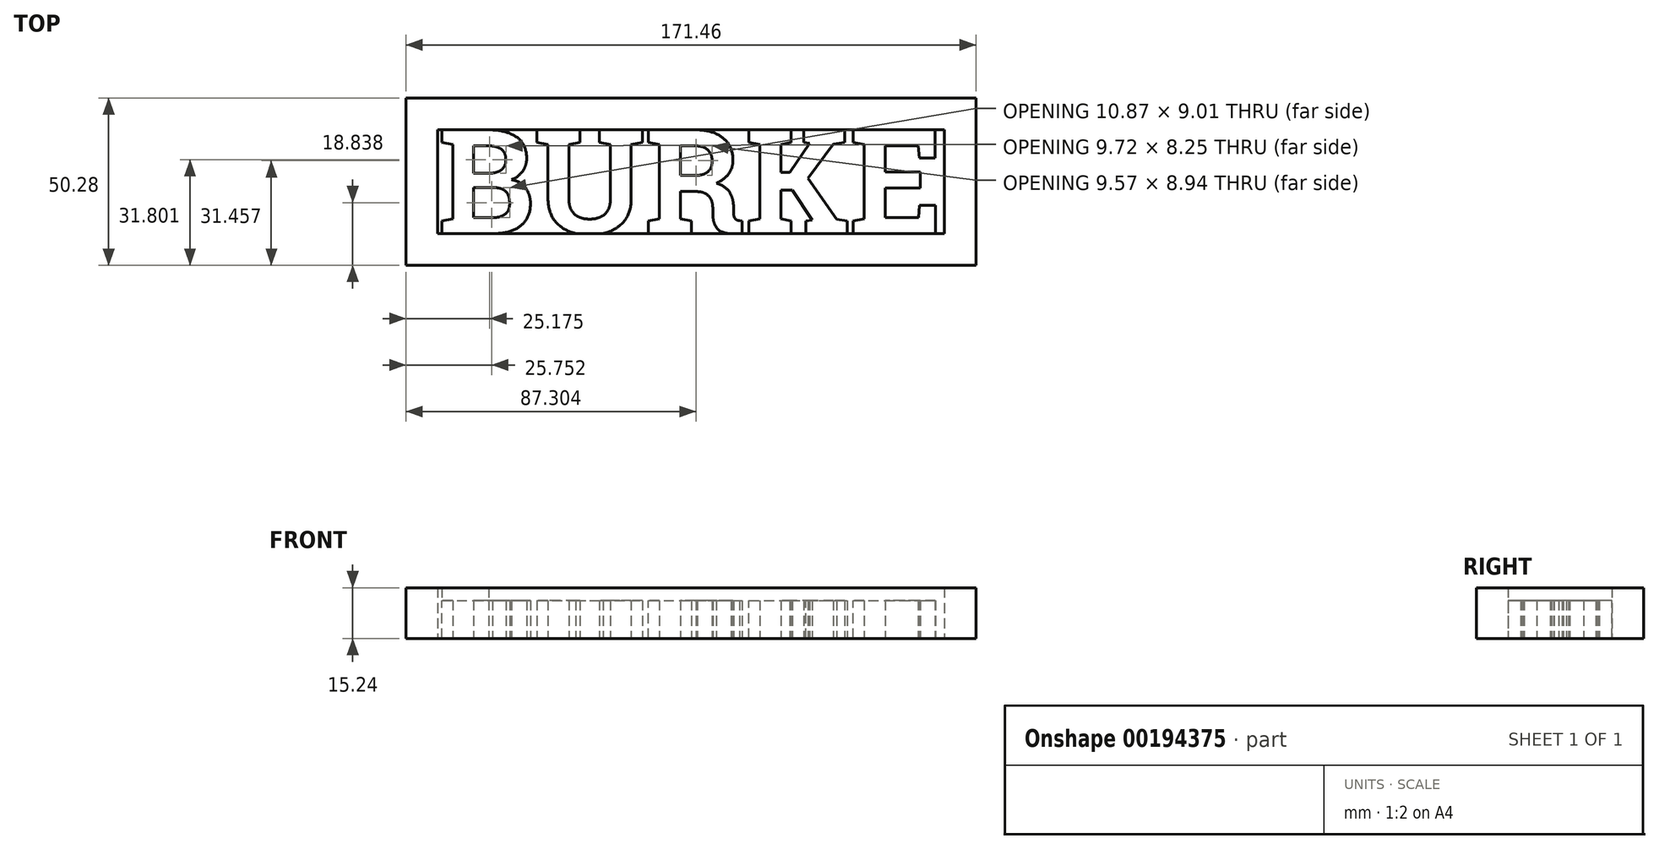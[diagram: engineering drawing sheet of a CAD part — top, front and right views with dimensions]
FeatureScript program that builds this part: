
annotation { "Feature Type Name" : "Feature", "Feature Type Description" : "" }
export const myFeature = defineFeature(function(context is Context, id is Id, definition is map)
    precondition{}
    {
        {
            var Q0;
            Q0=qCreatedBy(makeId("Top.planeOp"),FACE);
            var sketch = newSketch(context, id + "F0", { "sketchPlane" : qUnion([Q0])});
            skLineSegment(sketch, "E0.bottom", {"start": v(0, 0) * mm, "end": v(152.4, 0) * mm});
            skLineSegment(sketch, "E0.top", {"start": v(0, 9.53) * mm, "end": v(152.4, 9.53) * mm});
            skLineSegment(sketch, "E0.left", {"start": v(0, 0) * mm, "end": v(0, 9.53) * mm});
            skLineSegment(sketch, "E0.right", {"start": v(152.4, 0) * mm, "end": v(152.4, 9.53) * mm});
            skText(sketch, "E1", { "text": "BURKE", "fontName": "RobotoSlab-Bold.ttf"});
            const initialGuessF0  = {"E1": [0, 0.00953, 1, 0, 0.03162]};
            skSetInitialGuess(sketch, initialGuessF0);
            skSolve(sketch);
        }
        {
            var Q0;
            Q0=qSketchRegion(id+"F0",true);
            extrude(context, id + "F1", {"entities" : qUnion([Q0]), "depth" : 11.43 * mm});
        }
        {
            var Q0;
            Q0=makeQuery(id+"F1.opExtrude","CAP_FACE",FACE,{"disambiguationData":[OSD([sQuery(id+"F0.wireOp",EDGE,"E0.bottom"),sQuery(id+"F0.wireOp",EDGE,"E0.top"),sQuery(id+"F0.wireOp",EDGE,"E0.left"),sQuery(id+"F0.wireOp",EDGE,"E0.right"),sQuery(id+"F0.wireOp",EDGE,"E1.sketch_text.stroke-0"),sQuery(id+"F0.wireOp",EDGE,"E1.sketch_text.stroke-1"),sQuery(id+"F0.wireOp",EDGE,"E1.sketch_text.stroke-2"),sQuery(id+"F0.wireOp",EDGE,"E1.sketch_text.stroke-3"),sQuery(id+"F0.wireOp",EDGE,"E1.sketch_text.stroke-4"),sQuery(id+"F0.wireOp",EDGE,"E1.sketch_text.stroke-5"),sQuery(id+"F0.wireOp",EDGE,"E1.sketch_text.stroke-6"),sQuery(id+"F0.wireOp",EDGE,"E1.sketch_text.stroke-7"),sQuery(id+"F0.wireOp",EDGE,"E1.sketch_text.stroke-8"),sQuery(id+"F0.wireOp",EDGE,"E1.sketch_text.stroke-9"),sQuery(id+"F0.wireOp",EDGE,"E1.sketch_text.stroke-10"),sQuery(id+"F0.wireOp",EDGE,"E1.sketch_text.stroke-11"),sQuery(id+"F0.wireOp",EDGE,"E1.sketch_text.stroke-12"),sQuery(id+"F0.wireOp",EDGE,"E1.sketch_text.stroke-13"),sQuery(id+"F0.wireOp",EDGE,"E1.sketch_text.stroke-14"),sQuery(id+"F0.wireOp",EDGE,"E1.sketch_text.stroke-15"),sQuery(id+"F0.wireOp",EDGE,"E1.sketch_text.stroke-16"),sQuery(id+"F0.wireOp",EDGE,"E1.sketch_text.stroke-17"),sQuery(id+"F0.wireOp",EDGE,"E1.sketch_text.stroke-18"),sQuery(id+"F0.wireOp",EDGE,"E1.sketch_text.stroke-19"),sQuery(id+"F0.wireOp",EDGE,"E1.sketch_text.stroke-20"),sQuery(id+"F0.wireOp",EDGE,"E1.sketch_text.stroke-21"),sQuery(id+"F0.wireOp",EDGE,"E1.sketch_text.stroke-22"),sQuery(id+"F0.wireOp",EDGE,"E1.sketch_text.stroke-23"),sQuery(id+"F0.wireOp",EDGE,"E1.sketch_text.stroke-24"),sQuery(id+"F0.wireOp",EDGE,"E1.sketch_text.stroke-25"),sQuery(id+"F0.wireOp",EDGE,"E1.sketch_text.stroke-26"),sQuery(id+"F0.wireOp",EDGE,"E1.sketch_text.stroke-27"),sQuery(id+"F0.wireOp",EDGE,"E1.sketch_text.stroke-28"),sQuery(id+"F0.wireOp",EDGE,"E1.sketch_text.stroke-29"),sQuery(id+"F0.wireOp",EDGE,"E1.sketch_text.stroke-30"),sQuery(id+"F0.wireOp",EDGE,"E1.sketch_text.stroke-31"),sQuery(id+"F0.wireOp",EDGE,"E1.sketch_text.stroke-32"),sQuery(id+"F0.wireOp",EDGE,"E1.sketch_text.stroke-33"),sQuery(id+"F0.wireOp",EDGE,"E1.sketch_text.stroke-34"),sQuery(id+"F0.wireOp",EDGE,"E1.sketch_text.stroke-35"),sQuery(id+"F0.wireOp",EDGE,"E1.sketch_text.stroke-36"),sQuery(id+"F0.wireOp",EDGE,"E1.sketch_text.stroke-37"),sQuery(id+"F0.wireOp",EDGE,"E1.sketch_text.stroke-38"),sQuery(id+"F0.wireOp",EDGE,"E1.sketch_text.stroke-39"),sQuery(id+"F0.wireOp",EDGE,"E1.sketch_text.stroke-40"),sQuery(id+"F0.wireOp",EDGE,"E1.sketch_text.stroke-42"),sQuery(id+"F0.wireOp",EDGE,"E1.sketch_text.stroke-43"),sQuery(id+"F0.wireOp",EDGE,"E1.sketch_text.stroke-44"),sQuery(id+"F0.wireOp",EDGE,"E1.sketch_text.stroke-45"),sQuery(id+"F0.wireOp",EDGE,"E1.sketch_text.stroke-46"),sQuery(id+"F0.wireOp",EDGE,"E1.sketch_text.stroke-47"),sQuery(id+"F0.wireOp",EDGE,"E1.sketch_text.stroke-48"),sQuery(id+"F0.wireOp",EDGE,"E1.sketch_text.stroke-50"),sQuery(id+"F0.wireOp",EDGE,"E1.sketch_text.stroke-51"),sQuery(id+"F0.wireOp",EDGE,"E1.sketch_text.stroke-52"),sQuery(id+"F0.wireOp",EDGE,"E1.sketch_text.stroke-53"),sQuery(id+"F0.wireOp",EDGE,"E1.sketch_text.stroke-54"),sQuery(id+"F0.wireOp",EDGE,"E1.sketch_text.stroke-55"),sQuery(id+"F0.wireOp",EDGE,"E1.sketch_text.stroke-56"),sQuery(id+"F0.wireOp",EDGE,"E1.sketch_text.stroke-57"),sQuery(id+"F0.wireOp",EDGE,"E1.sketch_text.stroke-58"),sQuery(id+"F0.wireOp",EDGE,"E1.sketch_text.stroke-59"),sQuery(id+"F0.wireOp",EDGE,"E1.sketch_text.stroke-60"),sQuery(id+"F0.wireOp",EDGE,"E1.sketch_text.stroke-62"),sQuery(id+"F0.wireOp",EDGE,"E1.sketch_text.stroke-63"),sQuery(id+"F0.wireOp",EDGE,"E1.sketch_text.stroke-64"),sQuery(id+"F0.wireOp",EDGE,"E1.sketch_text.stroke-65"),sQuery(id+"F0.wireOp",EDGE,"E1.sketch_text.stroke-66"),sQuery(id+"F0.wireOp",EDGE,"E1.sketch_text.stroke-67"),sQuery(id+"F0.wireOp",EDGE,"E1.sketch_text.stroke-68"),sQuery(id+"F0.wireOp",EDGE,"E1.sketch_text.stroke-69"),sQuery(id+"F0.wireOp",EDGE,"E1.sketch_text.stroke-70"),sQuery(id+"F0.wireOp",EDGE,"E1.sketch_text.stroke-71"),sQuery(id+"F0.wireOp",EDGE,"E1.sketch_text.stroke-72"),sQuery(id+"F0.wireOp",EDGE,"E1.sketch_text.stroke-73"),sQuery(id+"F0.wireOp",EDGE,"E1.sketch_text.stroke-75"),sQuery(id+"F0.wireOp",EDGE,"E1.sketch_text.stroke-76"),sQuery(id+"F0.wireOp",EDGE,"E1.sketch_text.stroke-77"),sQuery(id+"F0.wireOp",EDGE,"E1.sketch_text.stroke-78"),sQuery(id+"F0.wireOp",EDGE,"E1.sketch_text.stroke-79"),sQuery(id+"F0.wireOp",EDGE,"E1.sketch_text.stroke-80"),sQuery(id+"F0.wireOp",EDGE,"E1.sketch_text.stroke-81"),sQuery(id+"F0.wireOp",EDGE,"E1.sketch_text.stroke-82"),sQuery(id+"F0.wireOp",EDGE,"E1.sketch_text.stroke-83"),sQuery(id+"F0.wireOp",EDGE,"E1.sketch_text.stroke-84"),sQuery(id+"F0.wireOp",EDGE,"E1.sketch_text.stroke-85"),sQuery(id+"F0.wireOp",EDGE,"E1.sketch_text.stroke-86"),sQuery(id+"F0.wireOp",EDGE,"E1.sketch_text.stroke-87"),sQuery(id+"F0.wireOp",EDGE,"E1.sketch_text.stroke-88")])],"isStart":false});
            var sketch = newSketch(context, id + "F2", { "sketchPlane" : qUnion([Q0])});
            skLineSegment(sketch, "E2.bottom", {"start": v(0, 0) * mm, "end": v(152.4, 0) * mm});
            skLineSegment(sketch, "E2.top", {"start": v(0, 9.53) * mm, "end": v(152.4, 9.53) * mm});
            skLineSegment(sketch, "E2.left", {"start": v(0, 0) * mm, "end": v(0, 9.53) * mm});
            skLineSegment(sketch, "E2.right", {"start": v(152.4, 0) * mm, "end": v(152.4, 9.53) * mm});
            skSolve(sketch);
        }
        {
            var Q0;
            Q0=qSketchRegion(id+"F2",true);
            extrude(context, id + "F3", {"entities" : qUnion([Q0]), "operationType" : NewBodyOperationType.ADD, "depth" : 3.8 * mm});
        }
        {
            var Q0;
            Q0=makeQuery(id+"F1.opExtrude","CAP_FACE",FACE,{"disambiguationData":[OSD([sQuery(id+"F0.wireOp",EDGE,"E0.bottom"),sQuery(id+"F0.wireOp",EDGE,"E0.top"),sQuery(id+"F0.wireOp",EDGE,"E0.left"),sQuery(id+"F0.wireOp",EDGE,"E0.right"),sQuery(id+"F0.wireOp",EDGE,"E1.sketch_text.stroke-0"),sQuery(id+"F0.wireOp",EDGE,"E1.sketch_text.stroke-1"),sQuery(id+"F0.wireOp",EDGE,"E1.sketch_text.stroke-2"),sQuery(id+"F0.wireOp",EDGE,"E1.sketch_text.stroke-3"),sQuery(id+"F0.wireOp",EDGE,"E1.sketch_text.stroke-4"),sQuery(id+"F0.wireOp",EDGE,"E1.sketch_text.stroke-5"),sQuery(id+"F0.wireOp",EDGE,"E1.sketch_text.stroke-7"),sQuery(id+"F0.wireOp",EDGE,"E1.sketch_text.stroke-8"),sQuery(id+"F0.wireOp",EDGE,"E1.sketch_text.stroke-9"),sQuery(id+"F0.wireOp",EDGE,"E1.sketch_text.stroke-10"),sQuery(id+"F0.wireOp",EDGE,"E1.sketch_text.stroke-11"),sQuery(id+"F0.wireOp",EDGE,"E1.sketch_text.stroke-12"),sQuery(id+"F0.wireOp",EDGE,"E1.sketch_text.stroke-13"),sQuery(id+"F0.wireOp",EDGE,"E1.sketch_text.stroke-15"),sQuery(id+"F0.wireOp",EDGE,"E1.sketch_text.stroke-16"),sQuery(id+"F0.wireOp",EDGE,"E1.sketch_text.stroke-17"),sQuery(id+"F0.wireOp",EDGE,"E1.sketch_text.stroke-18"),sQuery(id+"F0.wireOp",EDGE,"E1.sketch_text.stroke-19"),sQuery(id+"F0.wireOp",EDGE,"E1.sketch_text.stroke-20"),sQuery(id+"F0.wireOp",EDGE,"E1.sketch_text.stroke-21"),sQuery(id+"F0.wireOp",EDGE,"E1.sketch_text.stroke-22"),sQuery(id+"F0.wireOp",EDGE,"E1.sketch_text.stroke-23"),sQuery(id+"F0.wireOp",EDGE,"E1.sketch_text.stroke-24"),sQuery(id+"F0.wireOp",EDGE,"E1.sketch_text.stroke-25"),sQuery(id+"F0.wireOp",EDGE,"E1.sketch_text.stroke-26"),sQuery(id+"F0.wireOp",EDGE,"E1.sketch_text.stroke-27"),sQuery(id+"F0.wireOp",EDGE,"E1.sketch_text.stroke-28"),sQuery(id+"F0.wireOp",EDGE,"E1.sketch_text.stroke-29"),sQuery(id+"F0.wireOp",EDGE,"E1.sketch_text.stroke-30"),sQuery(id+"F0.wireOp",EDGE,"E1.sketch_text.stroke-32"),sQuery(id+"F0.wireOp",EDGE,"E1.sketch_text.stroke-33"),sQuery(id+"F0.wireOp",EDGE,"E1.sketch_text.stroke-34"),sQuery(id+"F0.wireOp",EDGE,"E1.sketch_text.stroke-35"),sQuery(id+"F0.wireOp",EDGE,"E1.sketch_text.stroke-36"),sQuery(id+"F0.wireOp",EDGE,"E1.sketch_text.stroke-37"),sQuery(id+"F0.wireOp",EDGE,"E1.sketch_text.stroke-38"),sQuery(id+"F0.wireOp",EDGE,"E1.sketch_text.stroke-39"),sQuery(id+"F0.wireOp",EDGE,"E1.sketch_text.stroke-40"),sQuery(id+"F0.wireOp",EDGE,"E1.sketch_text.stroke-42"),sQuery(id+"F0.wireOp",EDGE,"E1.sketch_text.stroke-43"),sQuery(id+"F0.wireOp",EDGE,"E1.sketch_text.stroke-44"),sQuery(id+"F0.wireOp",EDGE,"E1.sketch_text.stroke-45"),sQuery(id+"F0.wireOp",EDGE,"E1.sketch_text.stroke-46"),sQuery(id+"F0.wireOp",EDGE,"E1.sketch_text.stroke-47"),sQuery(id+"F0.wireOp",EDGE,"E1.sketch_text.stroke-48"),sQuery(id+"F0.wireOp",EDGE,"E1.sketch_text.stroke-49"),sQuery(id+"F0.wireOp",EDGE,"E1.sketch_text.stroke-50"),sQuery(id+"F0.wireOp",EDGE,"E1.sketch_text.stroke-51"),sQuery(id+"F0.wireOp",EDGE,"E1.sketch_text.stroke-52"),sQuery(id+"F0.wireOp",EDGE,"E1.sketch_text.stroke-53"),sQuery(id+"F0.wireOp",EDGE,"E1.sketch_text.stroke-54"),sQuery(id+"F0.wireOp",EDGE,"E1.sketch_text.stroke-55"),sQuery(id+"F0.wireOp",EDGE,"E1.sketch_text.stroke-56"),sQuery(id+"F0.wireOp",EDGE,"E1.sketch_text.stroke-57"),sQuery(id+"F0.wireOp",EDGE,"E1.sketch_text.stroke-58"),sQuery(id+"F0.wireOp",EDGE,"E1.sketch_text.stroke-59"),sQuery(id+"F0.wireOp",EDGE,"E1.sketch_text.stroke-60"),sQuery(id+"F0.wireOp",EDGE,"E1.sketch_text.stroke-61"),sQuery(id+"F0.wireOp",EDGE,"E1.sketch_text.stroke-62"),sQuery(id+"F0.wireOp",EDGE,"E1.sketch_text.stroke-64"),sQuery(id+"F0.wireOp",EDGE,"E1.sketch_text.stroke-65"),sQuery(id+"F0.wireOp",EDGE,"E1.sketch_text.stroke-66"),sQuery(id+"F0.wireOp",EDGE,"E1.sketch_text.stroke-67")])],"isStart":true});
            var sketch = newSketch(context, id + "F4", { "sketchPlane" : qUnion([Q0])});
            skLineSegment(sketch, "E3.bottom", {"start": v(0, -40.75) * mm, "end": v(152.4, -40.75) * mm});
            skLineSegment(sketch, "E3.top", {"start": v(0, -50.28) * mm, "end": v(152.4, -50.28) * mm});
            skLineSegment(sketch, "E3.left", {"start": v(0, -40.75) * mm, "end": v(0, -50.28) * mm});
            skLineSegment(sketch, "E3.right", {"start": v(152.4, -40.75) * mm, "end": v(152.4, -50.28) * mm});
            skLineSegment(sketch, "E4.bottom", {"start": v(0, -50.28) * mm, "end": v(-9.52, -50.28) * mm});
            skLineSegment(sketch, "E4.top", {"start": v(0, 0) * mm, "end": v(-9.53, 0) * mm});
            skLineSegment(sketch, "E4.left", {"start": v(0, -50.28) * mm, "end": v(0, 0) * mm});
            skLineSegment(sketch, "E4.right", {"start": v(-9.52, -50.28) * mm, "end": v(-9.53, 0) * mm});
            skLineSegment(sketch, "E5.bottom", {"start": v(152.4, -50.28) * mm, "end": v(161.93, -50.28) * mm});
            skLineSegment(sketch, "E5.top", {"start": v(152.4, 0) * mm, "end": v(161.93, 0) * mm});
            skLineSegment(sketch, "E5.left", {"start": v(152.4, -50.28) * mm, "end": v(152.4, 0) * mm});
            skLineSegment(sketch, "E5.right", {"start": v(161.93, -50.28) * mm, "end": v(161.93, 0) * mm});
            skSolve(sketch);
        }
        {
            var Q0;
            Q0=makeQuery(id+"F4.imprint","IMPRINT",FACE,{"disambiguationData":[TD([[makeQuery(id+"F4.imprint","IMPRINT",EDGE,{"derivedFrom":sQuery(id+"F4.wireOp",EDGE,"E3.top")}),1.0]])]});
            var Q1;
            {var subQ5=sQuery(id+"F4.wireOp",EDGE,"E4.bottom");Q1=makeQuery(id+"F4.imprint","IMPRINT",FACE,{"disambiguationData":[TD([[makeQuery(id+"F4.imprint","IMPRINT",EDGE,{"derivedFrom":subQ5}),-1.0]])]});}
            var Q2;
            {var subQ4=sQuery(id+"F4.wireOp",EDGE,"E5.bottom");Q2=makeQuery(id+"F4.imprint","IMPRINT",FACE,{"disambiguationData":[TD([[makeQuery(id+"F4.imprint","IMPRINT",EDGE,{"derivedFrom":subQ4}),1.0]])]});}
            var Q3;
            Q3=makeQuery(id+"F3.opExtrude","CAP_FACE",FACE,{"disambiguationData":[OSD([sQuery(id+"F2.wireOp",EDGE,"E2.bottom"),sQuery(id+"F2.wireOp",EDGE,"E2.top"),sQuery(id+"F2.wireOp",EDGE,"E2.left"),sQuery(id+"F2.wireOp",EDGE,"E2.right")])],"isStart":false});
            extrude(context, id + "F5", {"entities" : qUnion([Q0, Q1, Q2]), "operationType" : NewBodyOperationType.ADD, "endBound" : BoundingType.UP_TO_SURFACE, "oppositeDirection" : true, "endBoundEntityFace" : qUnion([Q3]), "depth" : 25.4 * mm});
        }
    });
